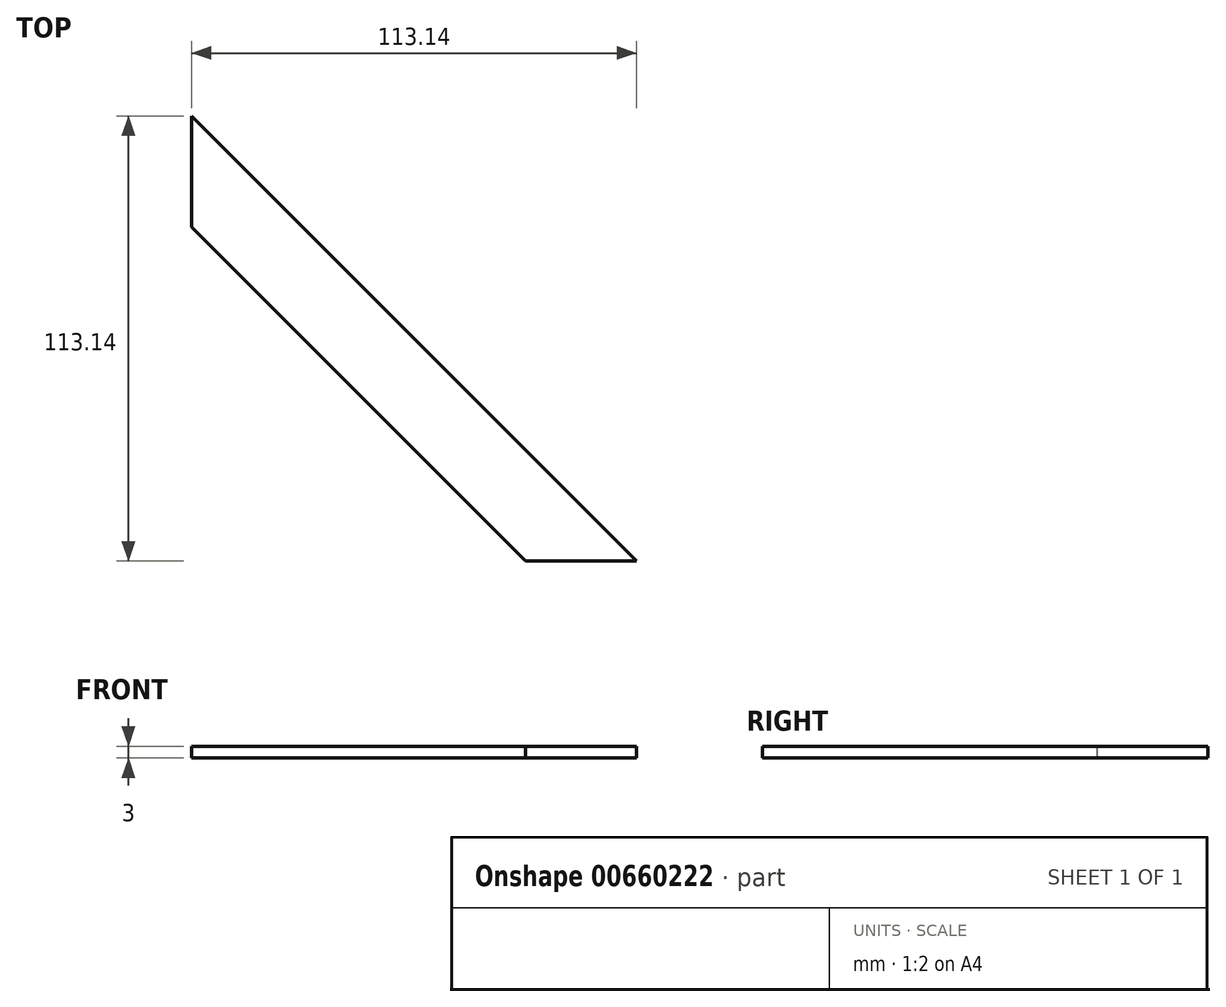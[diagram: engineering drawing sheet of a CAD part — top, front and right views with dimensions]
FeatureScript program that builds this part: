
annotation { "Feature Type Name" : "Feature", "Feature Type Description" : "" }
export const myFeature = defineFeature(function(context is Context, id is Id, definition is map)
    precondition{}
    {
        {
            var Q0;
            Q0=qCreatedBy(makeId("Top.planeOp"),FACE);
            var sketch = newSketch(context, id + "F0", { "sketchPlane" : qUnion([Q0])});
            skLineSegment(sketch, "E0", {"start": v(-490, 70) * mm, "end": v(-376.86, -43.14) * mm});
            skLineSegment(sketch, "E1", {"start": v(-490, 41.72) * mm, "end": v(-427.68, -20.6) * mm});
            skLineSegment(sketch, "E2", {"start": v(-490, 70) * mm, "end": v(-490, 41.72) * mm});
            skLineSegment(sketch, "E3", {"start": v(-376.86, -43.14) * mm, "end": v(-405.15, -43.14) * mm});
            skLineSegment(sketch, "E4", {"start": v(-427.68, -20.6) * mm, "end": v(-405.15, -43.14) * mm});
            skSolve(sketch);
        }
        {
            var Q0;
            Q0 = qSketchRegion(id + "F0", true);
            extrude(context, id + "F1", {"entities" : qUnion([Q0]), "depth" : 3 * mm, "offsetDistance" : 25 * mm});
        }
    });
